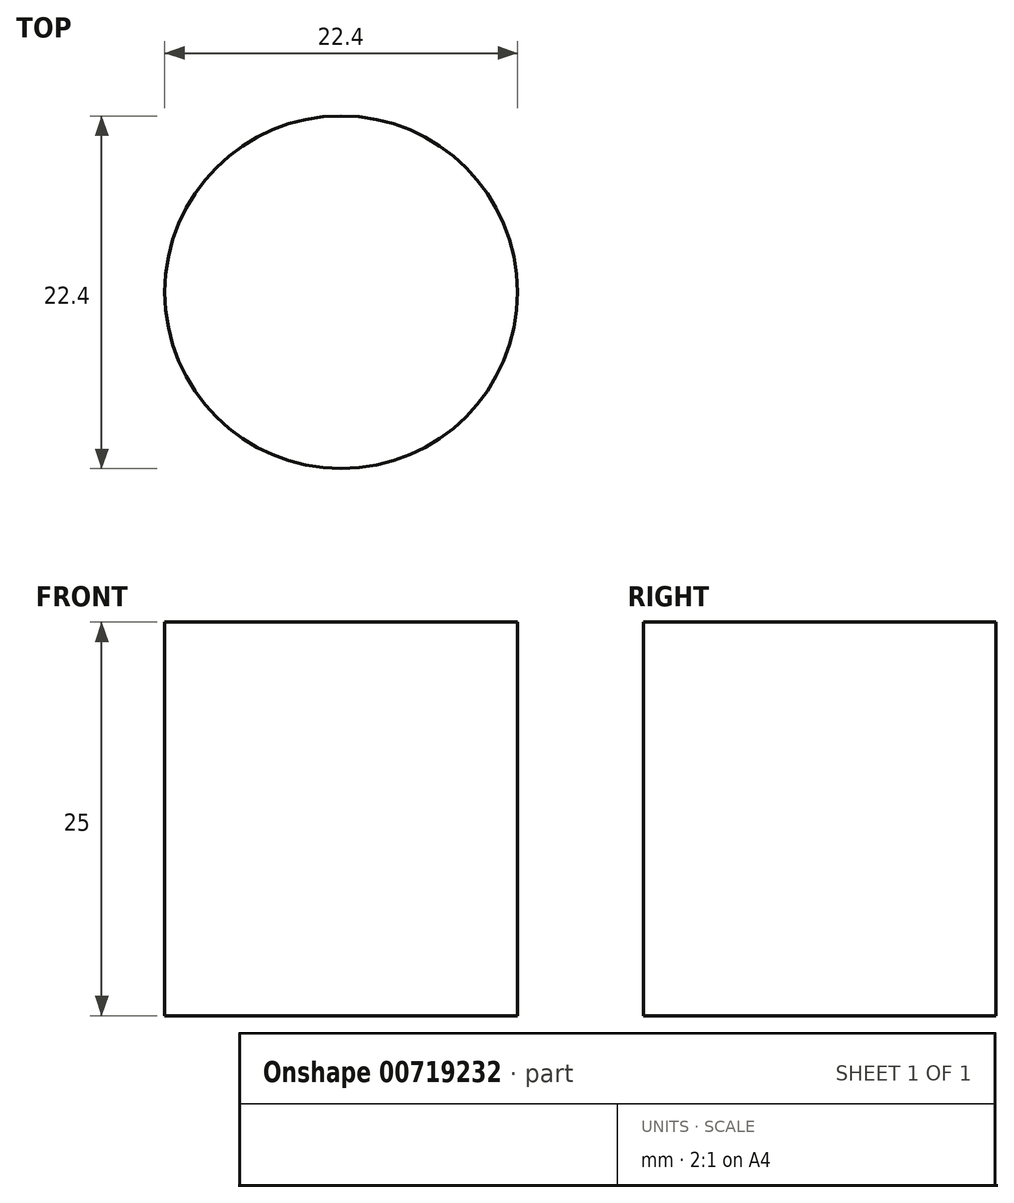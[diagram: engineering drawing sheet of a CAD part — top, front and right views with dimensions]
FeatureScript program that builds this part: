
annotation { "Feature Type Name" : "Feature", "Feature Type Description" : "" }
export const myFeature = defineFeature(function(context is Context, id is Id, definition is map)
    precondition{}
    {
        {
            var Q0;
            Q0=qCreatedBy(makeId("Top.planeOp"),FACE);
            var sketch = newSketch(context, id + "F0", { "sketchPlane" : qUnion([Q0])});
            skCircle(sketch, "E0", {"center": v(0, 0) * mm, "radius": 11.2 * mm});
            skSolve(sketch);
        }
        {
            var Q0;
            Q0=sQuery(id+"F0.wireOp",EDGE,"E0");
            extrude(context, id + "F1", {"bodyType" : ToolBodyType.SURFACE, "surfaceEntities" : qUnion([Q0]), "depth" : 25 * mm, "offsetDistance" : 25 * mm});
        }
    });
